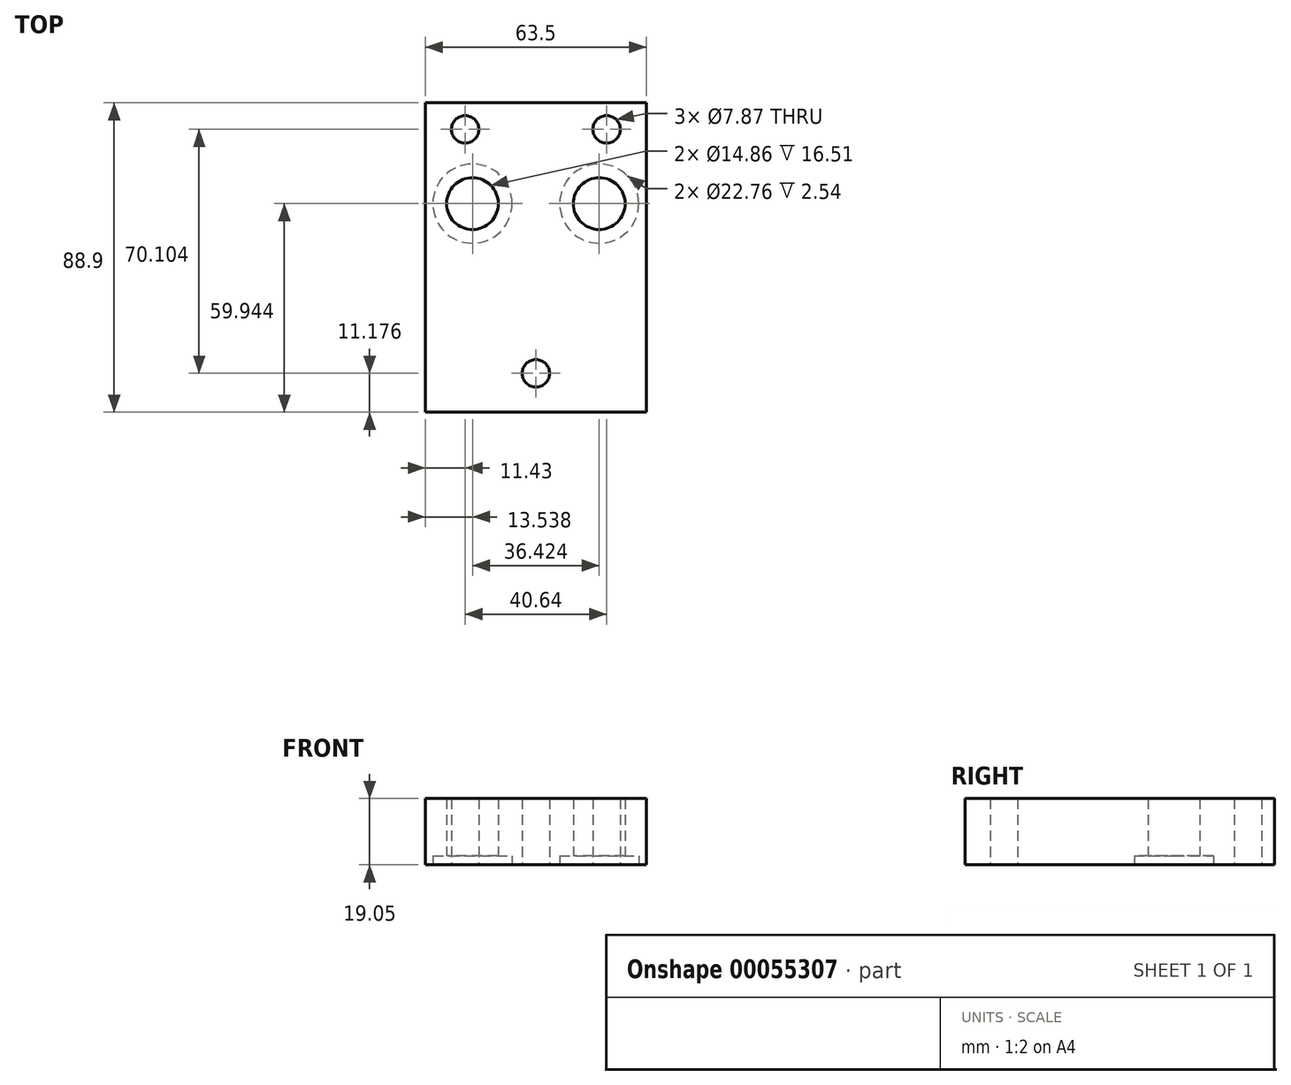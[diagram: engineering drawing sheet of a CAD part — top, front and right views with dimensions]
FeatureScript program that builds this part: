
annotation { "Feature Type Name" : "Feature", "Feature Type Description" : "" }
export const myFeature = defineFeature(function(context is Context, id is Id, definition is map)
    precondition{}
    {
        {
            var Q0;
            Q0=qCreatedBy(makeId("Top.planeOp"),FACE);
            var sketch = newSketch(context, id + "F0", { "sketchPlane" : qUnion([Q0])});
            skLineSegment(sketch, "E0.bottom", {"start": v(0, 0) * mm, "end": v(63.5, 0) * mm});
            skLineSegment(sketch, "E0.top", {"start": v(0, 88.9) * mm, "end": v(63.5, 88.9) * mm});
            skLineSegment(sketch, "E0.left", {"start": v(0, 0) * mm, "end": v(0, 88.9) * mm});
            skLineSegment(sketch, "E0.right", {"start": v(63.5, 0) * mm, "end": v(63.5, 88.9) * mm});
            skCircle(sketch, "E1", {"center": v(11.43, 81.28) * mm, "radius": 3.94 * mm});
            skCircle(sketch, "E2", {"center": v(52.07, 81.28) * mm, "radius": 3.94 * mm});
            skCircle(sketch, "E3", {"center": v(31.75, 11.18) * mm, "radius": 3.94 * mm});
            skCircle(sketch, "E4", {"center": v(13.54, 59.94) * mm, "radius": 7.43 * mm});
            skCircle(sketch, "E5", {"center": v(49.96, 59.94) * mm, "radius": 7.43 * mm});
            skSolve(sketch);
        }
        {
            var Q0;
            Q0=makeQuery(id+"F0.imprint","IMPRINT",FACE,{"disambiguationData":[TD([[makeQuery(id+"F0.imprint","IMPRINT",EDGE,{"derivedFrom":sQuery(id+"F0.wireOp",EDGE,"E0.bottom")}),1.0]])]});
            extrude(context, id + "F1", {"entities" : qUnion([Q0]), "depth" : 19.05 * mm});
        }
        {
            var Q0;
            Q0=makeQuery(id+"F1.opExtrude","CAP_FACE",FACE,{"disambiguationData":[OSD([sQuery(id+"F0.wireOp",EDGE,"E0.bottom"),sQuery(id+"F0.wireOp",EDGE,"E0.top"),sQuery(id+"F0.wireOp",EDGE,"E0.left"),sQuery(id+"F0.wireOp",EDGE,"E0.right"),sQuery(id+"F0.wireOp",EDGE,"E1"),sQuery(id+"F0.wireOp",EDGE,"E2"),sQuery(id+"F0.wireOp",EDGE,"E3"),sQuery(id+"F0.wireOp",EDGE,"E4"),sQuery(id+"F0.wireOp",EDGE,"E5")])],"isStart":true});
            var sketch = newSketch(context, id + "F2", { "sketchPlane" : qUnion([Q0])});
            skCircle(sketch, "E6", {"center": v(49.96, -59.94) * mm, "radius": 11.38 * mm});
            skCircle(sketch, "E7", {"center": v(13.54, -59.94) * mm, "radius": 11.38 * mm});
            skSolve(sketch);
        }
        {
            var Q0;
            Q0=makeQuery(id+"F2.imprint","IMPRINT",FACE,{"disambiguationData":[TD([[makeQuery(id+"F2.imprint","IMPRINT",EDGE,{"derivedFrom":sQuery(id+"F2.wireOp",EDGE,"E6")}),1.0]])]});
            var Q1;
            Q1=makeQuery(id+"F2.imprint","IMPRINT",FACE,{"disambiguationData":[TD([[makeQuery(id+"F2.imprint","IMPRINT",EDGE,{"derivedFrom":sQuery(id+"F2.wireOp",EDGE,"E7")}),1.0]])]});
            extrude(context, id + "F3", {"entities" : qUnion([Q0, Q1]), "operationType" : NewBodyOperationType.REMOVE, "oppositeDirection" : true, "depth" : 2.54 * mm});
        }
        {
            var Q0;
            Q0=makeQuery(id+"F1.opExtrude","SWEPT_BODY",BODY,{"disambiguationData":[OSD([sQuery(id+"F0.wireOp",EDGE,"E0.bottom"),sQuery(id+"F0.wireOp",EDGE,"E0.top"),sQuery(id+"F0.wireOp",EDGE,"E0.left"),sQuery(id+"F0.wireOp",EDGE,"E0.right"),sQuery(id+"F0.wireOp",EDGE,"E1"),sQuery(id+"F0.wireOp",EDGE,"E2"),sQuery(id+"F0.wireOp",EDGE,"E3"),sQuery(id+"F0.wireOp",EDGE,"E4"),sQuery(id+"F0.wireOp",EDGE,"E5")])]});
            transform(context, id + "F4", {"entities" : qUnion([Q0]), "transformType" : TransformType.TRANSLATION_3D, "dx" : -152.4 * mm, "dy" : 0 * mm, "dz" : 0 * mm, "makeCopy" : true});
        }
        {
            var Q0;
            Q0=makeQuery(id+"F4.opPattern","COPY",BODY,{"derivedFrom":makeQuery(id+"F1.opExtrude","SWEPT_BODY",BODY,{"disambiguationData":[OSD([sQuery(id+"F0.wireOp",EDGE,"E0.bottom"),sQuery(id+"F0.wireOp",EDGE,"E0.top"),sQuery(id+"F0.wireOp",EDGE,"E0.left"),sQuery(id+"F0.wireOp",EDGE,"E0.right"),sQuery(id+"F0.wireOp",EDGE,"E1"),sQuery(id+"F0.wireOp",EDGE,"E2"),sQuery(id+"F0.wireOp",EDGE,"E3"),sQuery(id+"F0.wireOp",EDGE,"E4"),sQuery(id+"F0.wireOp",EDGE,"E5")])]}),"instanceName":"1"});
            deleteBodies(context, id + "F5", {"entities" : qUnion([Q0])});
        }
    });
